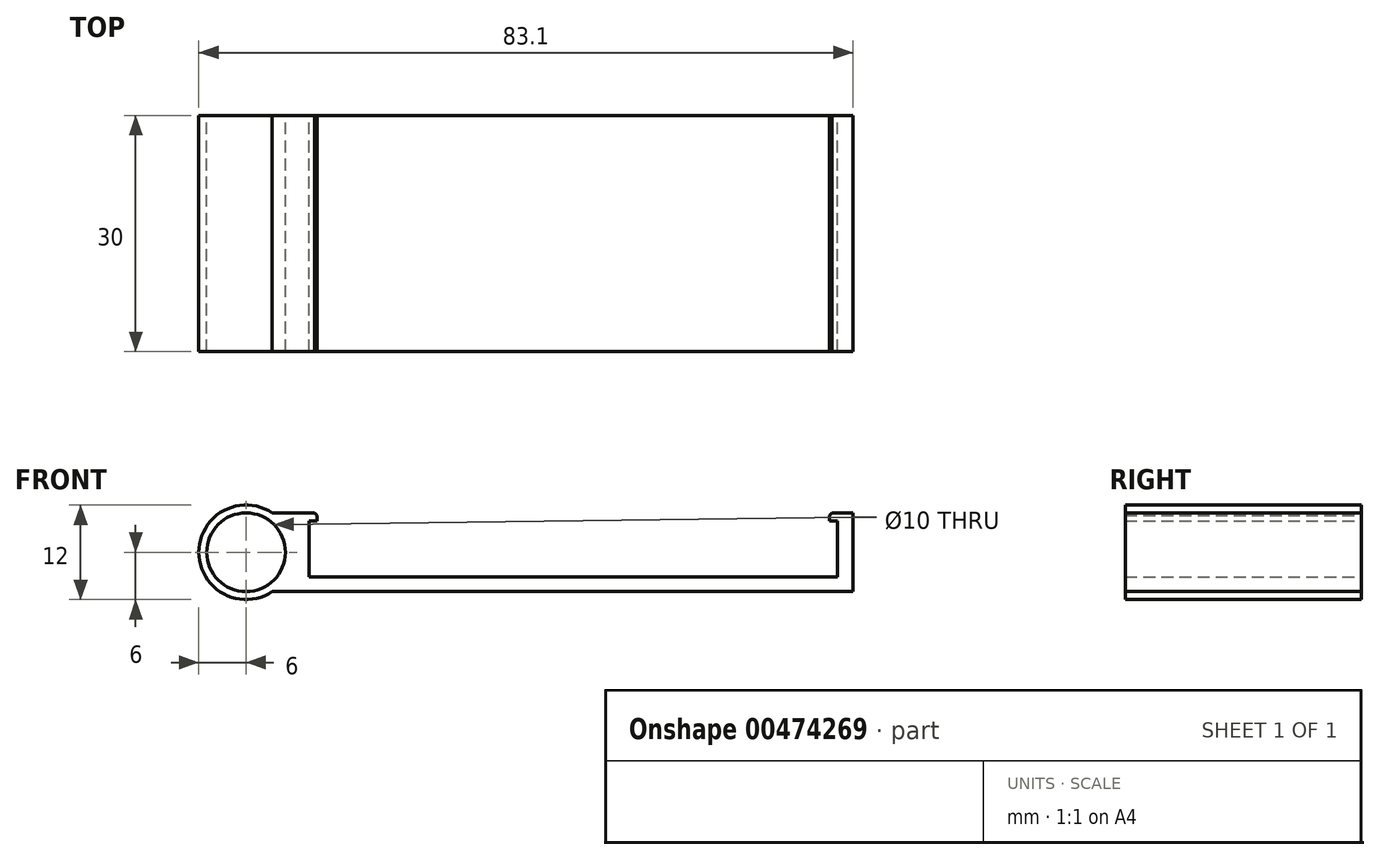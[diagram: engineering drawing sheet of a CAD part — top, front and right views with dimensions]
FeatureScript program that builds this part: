
annotation { "Feature Type Name" : "Feature", "Feature Type Description" : "" }
export const myFeature = defineFeature(function(context is Context, id is Id, definition is map)
    precondition{}
    {
        {
            var Q0;
            Q0=qCreatedBy(makeId("Front.planeOp"),FACE);
            var sketch = newSketch(context, id + "F0", { "sketchPlane" : qUnion([Q0])});
            skLineSegment(sketch, "E0", {"start": v(0, 0) * mm, "end": v(3, 0) * mm});
            skLineSegment(sketch, "E1", {"start": v(3, 0) * mm, "end": v(3, -1) * mm});
            skLineSegment(sketch, "E2", {"start": v(3, -1) * mm, "end": v(2, -1) * mm});
            skLineSegment(sketch, "E3", {"start": v(2, -1) * mm, "end": v(2, -8.1) * mm});
            skLineSegment(sketch, "E4", {"start": v(2, -8.1) * mm, "end": v(69.1, -8.1) * mm});
            skLineSegment(sketch, "E5", {"start": v(69.1, -8.1) * mm, "end": v(69.1, -1) * mm});
            skLineSegment(sketch, "E6", {"start": v(69.1, -1) * mm, "end": v(68.1, -1) * mm});
            skLineSegment(sketch, "E7", {"start": v(68.1, -1) * mm, "end": v(68.1, 0) * mm});
            skLineSegment(sketch, "E8", {"start": v(68.1, 0) * mm, "end": v(71.1, 0) * mm});
            skLineSegment(sketch, "E9", {"start": v(71.1, 0) * mm, "end": v(71.1, -10) * mm});
            skLineSegment(sketch, "E10", {"start": v(71.1, -10) * mm, "end": v(0, -10) * mm});
            skArc(sketch, "E11", {"start": v(-2.68, 0) * mm, "mid": v(-12, -5) * mm, "end": v(-2.68, -10) * mm});
            skPoint(sketch, "E11.centerSnap0", {"position": v(0, -5) * mm});
            skPoint(sketch, "E11.perimeterSnap0", {"position": v(0, -5) * mm});
            skPoint(sketch, "E11.perimeterSnap1", {"position": v(2, -4.55) * mm});
            skLineSegment(sketch, "E12", {"start": v(0, 0) * mm, "end": v(-2.68, 0) * mm});
            skLineSegment(sketch, "E13", {"start": v(0, -10) * mm, "end": v(-2.68, -10) * mm});
            skCircle(sketch, "E14", {"center": v(-6, -5) * mm, "radius": 5 * mm});
            skSolve(sketch);
        }
        {
            var Q0;
            Q0=makeQuery(id+"F0.imprint","IMPRINT",FACE,{"disambiguationData":[TD([[makeQuery(id+"F0.imprint","IMPRINT",EDGE,{"derivedFrom":sQuery(id+"F0.wireOp",EDGE,"E0")}),-1.0]])]});
            extrude(context, id + "F1", {"entities" : qUnion([Q0]), "depth" : 30 * mm});
        }
        {
            var Q0;
            Q0=makeQuery(id+"F1.opExtrude","SWEPT_EDGE",EDGE,{"disambiguationData":[OSD([sQuery(id+"F0.wireOp",EDGE,"E7"),sQuery(id+"F0.wireOp",EDGE,"E8")])]});
            var Q1;
            Q1=makeQuery(id+"F1.opExtrude","SWEPT_EDGE",EDGE,{"disambiguationData":[OSD([sQuery(id+"F0.wireOp",EDGE,"E0"),sQuery(id+"F0.wireOp",EDGE,"E1")])]});
            chamfer(context, id + "F2", {"entities" : qUnion([Q0, Q1]), "width" : .3 * mm, "tangentPropagation" : true});
        }
    });
